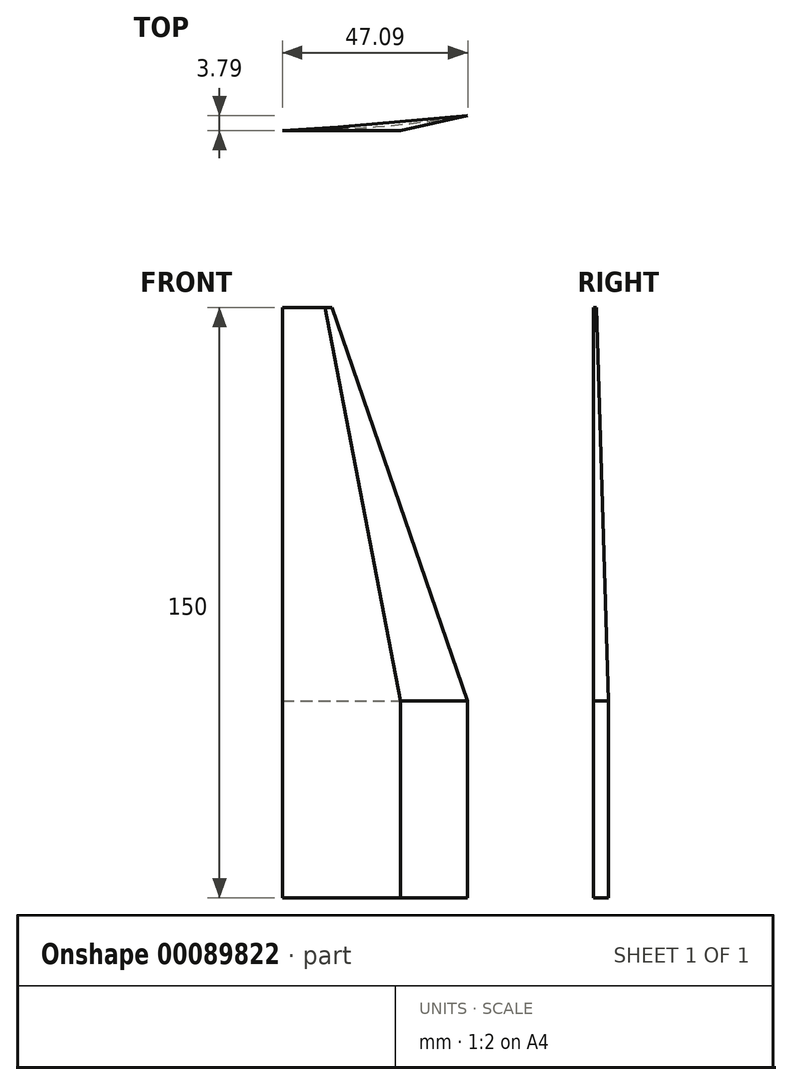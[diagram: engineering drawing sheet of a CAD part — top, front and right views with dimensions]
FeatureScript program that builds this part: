
annotation { "Feature Type Name" : "Feature", "Feature Type Description" : "" }
export const myFeature = defineFeature(function(context is Context, id is Id, definition is map)
    precondition{}
    {
        {
            var Q0;
            Q0=qCreatedBy(makeId("Top.planeOp"),FACE);
            var sketch = newSketch(context, id + "F0", { "sketchPlane" : qUnion([Q0])});
            skLineSegment(sketch, "E0.bottom", {"start": v(-30, 0) * mm, "end": v(0, 0) * mm});
            skLineSegment(sketch, "E0.top", {"start": v(-30, 0) * mm, "end": v(0, 0) * mm});
            skLineSegment(sketch, "E0.left", {"start": v(-30, 0) * mm, "end": v(-30, 0) * mm});
            skLineSegment(sketch, "E0.right", {"start": v(0, 0) * mm, "end": v(0, 0) * mm});
            skLineSegment(sketch, "E1", {"start": v(0, 0) * mm, "end": v(17.09, 3.79) * mm});
            skArc(sketch, "E2", {"start": v(-30, 0) * mm, "mid": v(-6.38, 0.95) * mm, "end": v(17.09, 3.79) * mm});
            skSolve(sketch);
        }
        {
            var Q0;
            Q0=qCreatedBy(makeId("Top.planeOp"),FACE);
            cPlane(context, id + "F1", {"entities" : qUnion([Q0]), "cplaneType" : CPlaneType.OFFSET, "offset" : 150 * mm, "width" : 152.4 * mm, "height" : 152.4 * mm});
        }
        {
            var Q0;
            Q0=qCreatedBy(id+"F1.planeOp",FACE);
            var sketch = newSketch(context, id + "F2", { "sketchPlane" : qUnion([Q0])});
            skLineSegment(sketch, "E3", {"start": v(-30, 0) * mm, "end": v(-19.21, 0) * mm});
            skLineSegment(sketch, "E4", {"start": v(-19.21, 0) * mm, "end": v(-17.35, 0.66) * mm});
            skLineSegment(sketch, "E5", {"start": v(-17.35, 0.66) * mm, "end": v(-30, 0) * mm});
            skSolve(sketch);
        }
        {
            var Q0;
            Q0=qCreatedBy(makeId("Top.planeOp"),FACE);
            cPlane(context, id + "F3", {"entities" : qUnion([Q0]), "cplaneType" : CPlaneType.OFFSET, "offset" : 50 * mm, "width" : 152.4 * mm, "height" : 152.4 * mm});
        }
        {
            var Q0;
            Q0=qCreatedBy(id+"F3.planeOp",FACE);
            var sketch = newSketch(context, id + "F4", { "sketchPlane" : qUnion([Q0])});
            skLineSegment(sketch, "E6", {"start": v(-30, 0) * mm, "end": v(0, 0) * mm});
            skLineSegment(sketch, "E7", {"start": v(0, 0) * mm, "end": v(17.09, 3.79) * mm});
            skArc(sketch, "E8", {"start": v(-30, 0) * mm, "mid": v(-6.38, 0.95) * mm, "end": v(17.09, 3.79) * mm});
            skSolve(sketch);
        }
        {
            var Q0;
            Q0=qSketchRegion(id+"F0",true);
            var Q1;
            Q1=qSketchRegion(id+"F4",true);
            loft(context, id + "F5", {"sheetProfilesArray" : [{ "sheetProfileEntities" : qUnion([Q0]) }, { "sheetProfileEntities" : qUnion([Q1]) }]});
        }
        {
            var Q1;
            Q1=qSketchRegion(id+"F4",true);
            var Q2;
            Q2=qSketchRegion(id+"F2",true);
            loft(context, id + "F6", {"operationType" : NewBodyOperationType.ADD, "sheetProfilesArray" : [{ "sheetProfileEntities" : qUnion([Q1]) }, { "sheetProfileEntities" : qUnion([Q2]) }]});
        }
    });
